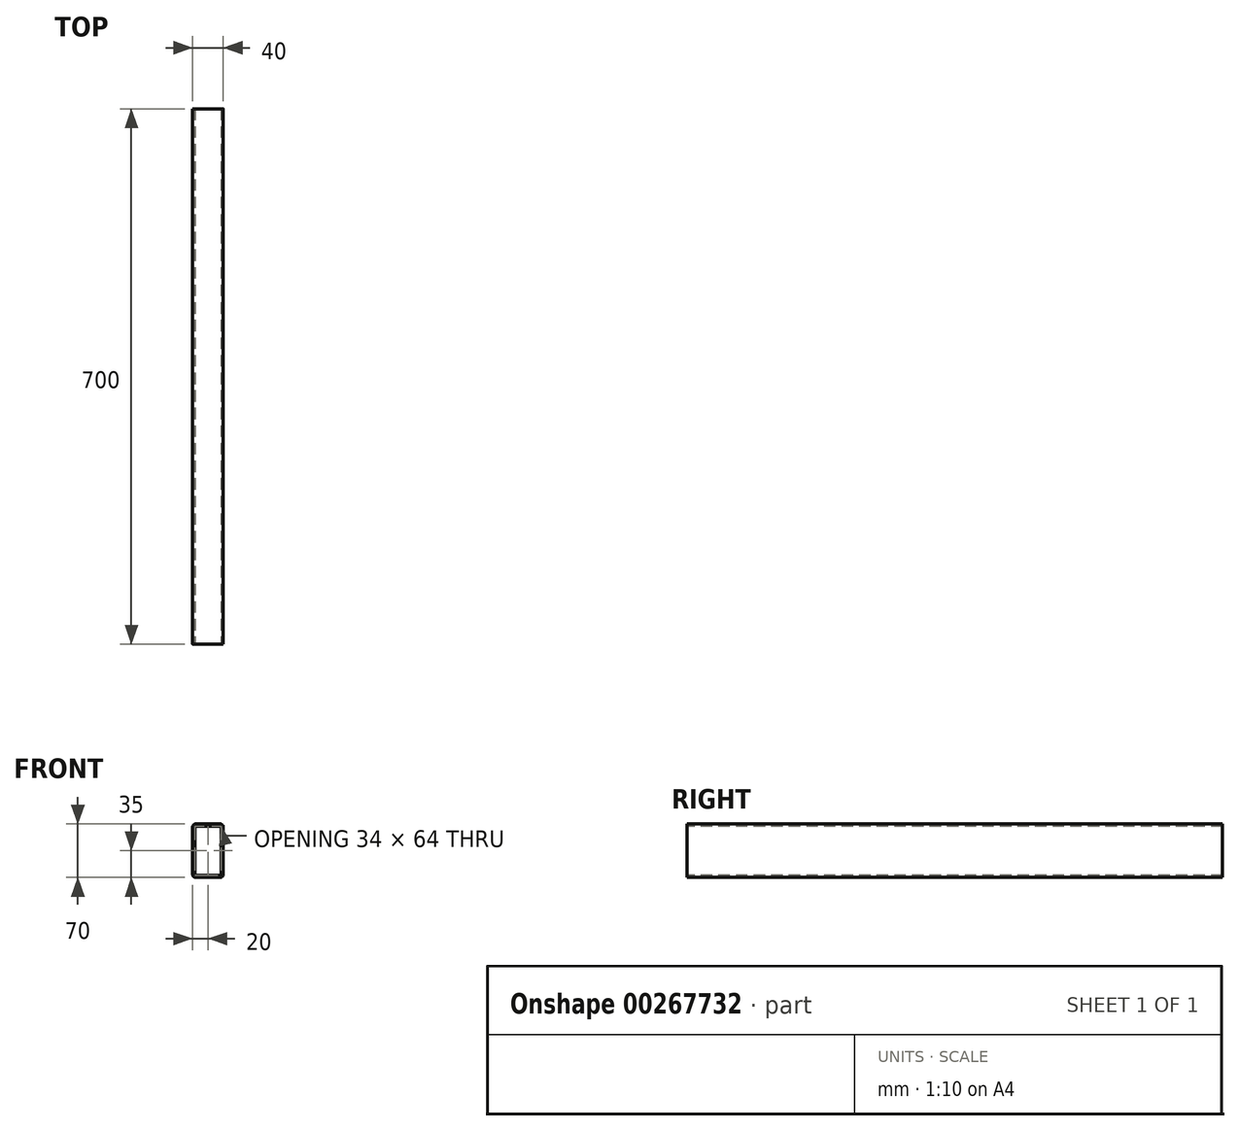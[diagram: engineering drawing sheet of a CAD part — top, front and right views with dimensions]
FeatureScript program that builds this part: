
annotation { "Feature Type Name" : "Feature", "Feature Type Description" : "" }
export const myFeature = defineFeature(function(context is Context, id is Id, definition is map)
    precondition{}
    {
        {
            var Q0;
            Q0=qCreatedBy(makeId("Front.planeOp"),FACE);
            var sketch = newSketch(context, id + "F0", { "sketchPlane" : qUnion([Q0])});
            skLineSegment(sketch, "E0.bottom", {"start": v(16, -35) * mm, "end": v(-16, -35) * mm});
            skLineSegment(sketch, "E0.top", {"start": v(16, 35) * mm, "end": v(-16, 35) * mm});
            skLineSegment(sketch, "E0.left", {"start": v(20, -31) * mm, "end": v(20, 31) * mm});
            skLineSegment(sketch, "E0.right", {"start": v(-20, -31) * mm, "end": v(-20, 31) * mm});
            skPoint(sketch, "E0.middle", {"position": v(0, 0) * mm});
            skPoint(sketch, "E1.visualSharp", {"position": v(-20, 35) * mm});
            skArc(sketch, "E1.filletArc", {"start": v(-16, 35) * mm, "mid": v(-18.83, 33.83) * mm, "end": v(-20, 31) * mm});
            skPoint(sketch, "E2.visualSharp", {"position": v(20, 35) * mm});
            skArc(sketch, "E2.filletArc", {"start": v(20, 31) * mm, "mid": v(18.83, 33.83) * mm, "end": v(16, 35) * mm});
            skPoint(sketch, "E3.visualSharp", {"position": v(20, -35) * mm});
            skArc(sketch, "E3.filletArc", {"start": v(16, -35) * mm, "mid": v(18.83, -33.83) * mm, "end": v(20, -31) * mm});
            skPoint(sketch, "E4.visualSharp", {"position": v(-20, -35) * mm});
            skArc(sketch, "E4.filletArc", {"start": v(-20, -31) * mm, "mid": v(-18.83, -33.83) * mm, "end": v(-16, -35) * mm});
            skArc(sketch, "E5.0", {"start": v(-17, -31) * mm, "mid": v(-16.7, -31.7) * mm, "end": v(-16, -32) * mm});
            skLineSegment(sketch, "E5.1", {"start": v(16, -32) * mm, "end": v(-16, -32) * mm});
            skLineSegment(sketch, "E5.2", {"start": v(-17, -31) * mm, "end": v(-17, 31) * mm});
            skArc(sketch, "E5.3", {"start": v(16, -32) * mm, "mid": v(16.7, -31.7) * mm, "end": v(17, -31) * mm});
            skArc(sketch, "E5.4", {"start": v(-16, 32) * mm, "mid": v(-16.7, 31.7) * mm, "end": v(-17, 31) * mm});
            skLineSegment(sketch, "E5.5", {"start": v(16, 32) * mm, "end": v(-16, 32) * mm});
            skArc(sketch, "E5.6", {"start": v(17, 31) * mm, "mid": v(16.7, 31.7) * mm, "end": v(16, 32) * mm});
            skLineSegment(sketch, "E5.7", {"start": v(17, -31) * mm, "end": v(17, 31) * mm});
            skSolve(sketch);
        }
        {
            var Q0;
            Q0=qSketchRegion(id+"F0",true);
            extrude(context, id + "F1", {"entities" : qUnion([Q0]), "oppositeDirection" : true, "depth" : 700 * mm});
        }
    });
